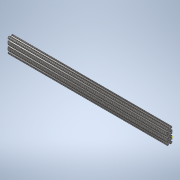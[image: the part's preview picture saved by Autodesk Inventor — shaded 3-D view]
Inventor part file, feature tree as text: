
AUTODESK INVENTOR PART (.ipt)
format: ipt  version: 2020 (Build 240168000, 168)  size: 395,264 bytes
history: native  units: in
note: dims shown in document units (in); Inventor stores cm internally (conversion verified against a paired STEP export)
features: sketch x2, extrude x1
ambient origin geometry x8: Origin, YZ Plane, XZ Plane, XY Plane, X Axis, Y Axis, Z Axis, Center Point
bodies: Solid1 (feature_tree)
feature tree (3):
  extrude  "Extrusion1"  [1 undecoded]
  sketch  "Sketch2"
  sketch  "Sketch1"  dims[d0=32.0in d1=0.0in]
note: 1 required parameter value undecoded (feature->parameter linkage not recoverable at this tier; creation-order binding heuristic only, values carry confidence <= 0.55)
